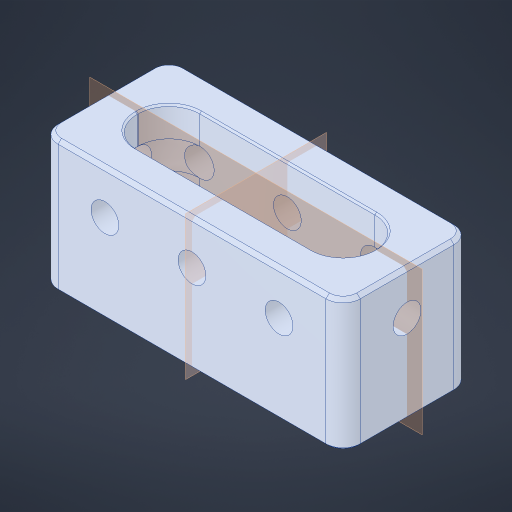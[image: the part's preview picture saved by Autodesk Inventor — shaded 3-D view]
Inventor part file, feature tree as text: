
AUTODESK INVENTOR PART (.ipt)
format: ipt  version: 2023.4 (Build 274418000, 418)  size: 363,520 bytes
history: native  units: in
note: dims shown in document units (in); Inventor stores cm internally (conversion verified against a paired STEP export)
features: sketch x4, hole x3, projected_geometry x2, extrude x1, chamfer x1
ambient origin geometry x8: Origin, YZ Plane, XZ Plane, XY Plane, X Axis, Y Axis, Z Axis, Center Point
bodies: Solid1 (feature_tree)
feature tree (11):
  extrude  "Extrusion1"  Depth=1.0in TaperAngle=0.0deg
  hole  "Hole1"  [1 undecoded]
  hole  "Hole2"  [1 undecoded]
  hole  "Hole3"  [1 undecoded]
  sketch  "Sketch1"  dims[d0=0.0625in d1=1.0in d2=0.0in]
  projected_geometry  "Projected Loop1"
  sketch  "Sketch2"  dims[d3=0.156in d4=0.38in d5=0.385in d6=0.25in d7=0.563in d8=1.0in d9=0.8108in]
  projected_geometry  "Projected Loop2"
  sketch  "Sketch3"  dims[d10=0.196in d11=0.5in d12=0.375in d13=0.25in d14=0.5635in d15=1.0in d16=0.8108in]
  sketch  "Sketch4"  dims[d17=0.156in d18=0.38in d19=0.385in d20=0.25in d21=0.563in d22=1.0in d23=0.8108in]
  chamfer  "Chamfer2"  [1 undecoded]
note: 4 required parameter values undecoded (feature->parameter linkage not recoverable at this tier; creation-order binding heuristic only, values carry confidence <= 0.55)
